# Revit family: final_Toilet-Top_Spud-American_Standard-Madera-2854111.020
name_source: partatom
category: Plumbing Fixtures
units: mm (PartAtom-declared; Revit-internal decimal feet)

## family parameters
Always vertical = No
Cut with Voids When Loaded = No
OmniClass Number = 23.45.05.21.11.11
OmniClass Title = Water Operated Water Closets
Part Type = Normal
Room Calculation Point = No
Round Connector Dimension = Use Diameter
Shared = Yes
Work Plane-Based = Yes

## types (1)
- 2854111.020
    10" Rough In = No
    12" Rough In = Yes
    3461001.020 Toilet Bowl = Yes
    6047111.002 Flush Valve = Yes
    ADA Compliant = Yes
    ASME A112.19.2M for Vitreous China Fixtures = Yes
    Assembly Code = D2010110
    Bowl Shape = Elongated
    CW Connection = Yes
    CWFU = 5
    CalGreen Compliant = Yes
    Cold Water Connection Diameter = 1"
    Compliance Certifications = Everclean, ASSE 1037 & ANSI/ASME A112.19.2
    Default Elevation = 0"
    Description = Madera™ Chair Height EverClean® Toilet System With Manual Piston Flush Valve, 1.1 gpf/4.2 Lpf
    EPA WaterSense® Certified = Yes
    Finish = Vitreous China-American Standard-020-White
    Finish- Flush Valve = Metal-American Standard-Brass-002-Polished Chrome
    Flow Rate = 25gpm (94.6 L/min.)
    Flush Rate = 1.1 gpf (4.2 Lpf) to 1.6 gpf  (6.0 Lpf)
    HW Connection = No
    HWFU = 0
    Height- Bowl = 16 1/2"
    Height- Flush Valve = 13 1/2"
    Installation Type = Floor Mounted
    Length = 28 1/4"
    Manufacturer = American Standard
    Material = Vitreous China-American Standard-020-White
    Model = 2854111.020
    Operating Pressure = 25 psi (flowing) - 80 psi (static)
    Overall Height = 30"
    Price = Prices may vary. Please consult Manufacturer Representative for most up-to-date price list.
    Product Documentation Link = https://americanstandard.box.com
    Product Page URL = https://www.americanstandard-us.com
    Revised Date = 12/01/2021
    Rough In Distance = 12"
    URL = http://www.americanstandard-us.com
    Vent Connection = No
    WFU = 5
    Warranty Information = 5 Year Limited Warranty on Fixture and Flush Valve
    Waste Connection = Yes
    Waste Connection Diameter = 2 1/8"
    Weight Lbs = 2,500 lbs (1,134 kg)
    Width = 14"
    Width- Toilet Seat = 14 3/8"

## geometry (parser evidence)
native form markers: Sweep x1
no freeform markers — native parametric forms only
